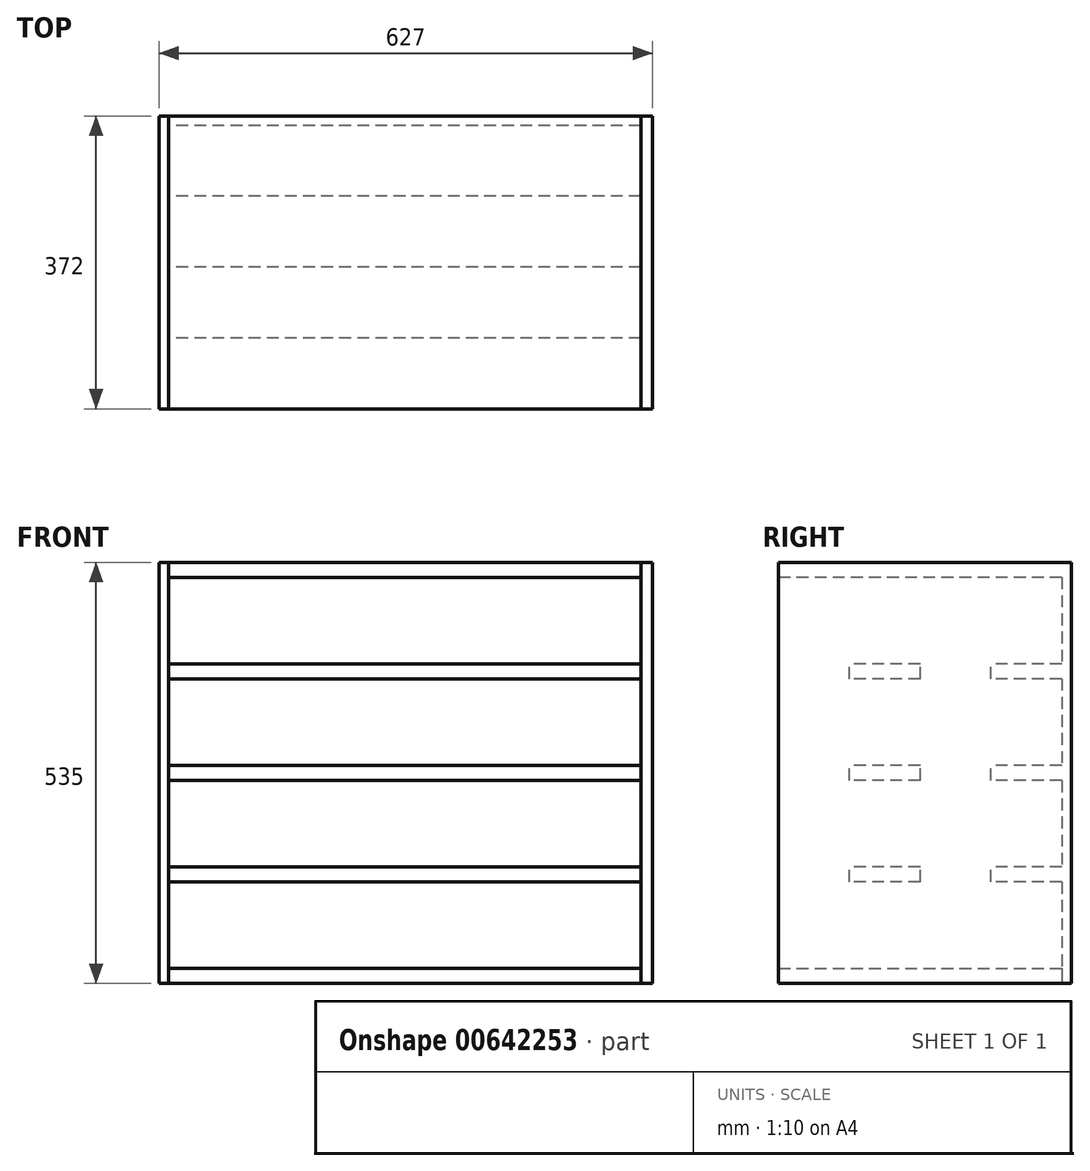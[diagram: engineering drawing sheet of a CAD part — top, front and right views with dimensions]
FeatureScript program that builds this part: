
annotation { "Feature Type Name" : "Feature", "Feature Type Description" : "" }
export const myFeature = defineFeature(function(context is Context, id is Id, definition is map)
    precondition{}
    {
        {
            var Q0;
            Q0=qCreatedBy(makeId("Right.planeOp"),FACE);
            var sketch = newSketch(context, id + "F0", { "sketchPlane" : qUnion([Q0])});
            skLineSegment(sketch, "E0.bottom", {"start": v(-360, 19) * mm, "end": v(0, 19) * mm});
            skLineSegment(sketch, "E0.top", {"start": v(-360, 0) * mm, "end": v(0, 0) * mm});
            skLineSegment(sketch, "E0.left", {"start": v(-360, 19) * mm, "end": v(-360, 0) * mm});
            skLineSegment(sketch, "E0.right", {"start": v(0, 19) * mm, "end": v(0, 0) * mm});
            skSolve(sketch);
        }
        {
            var Q0;
            Q0 = qSketchRegion(id + "F0", true);
            extrude(context, id + "F1", {"entities" : qUnion([Q0]), "depth" : 600 * mm, "offsetDistance" : 25.4 * mm});
        }
        {
            var Q0;
            Q0=qCreatedBy(makeId("Right.planeOp"),FACE);
            var sketch = newSketch(context, id + "F2", { "sketchPlane" : qUnion([Q0])});
            skLineSegment(sketch, "E1.bottom", {"start": v(0, 129) * mm, "end": v(-90, 129) * mm});
            skLineSegment(sketch, "E1.top", {"start": v(0, 148) * mm, "end": v(-90, 148) * mm});
            skLineSegment(sketch, "E1.right", {"start": v(-90, 129) * mm, "end": v(-90, 148) * mm});
            skLineSegment(sketch, "E2.0.1.0", {"start": v(-90, 258) * mm, "end": v(-90, 277) * mm});
            skLineSegment(sketch, "E2.0.1.1", {"start": v(0, 277) * mm, "end": v(-90, 277) * mm});
            skLineSegment(sketch, "E2.0.1.2", {"start": v(0, 258) * mm, "end": v(-90, 258) * mm});
            skLineSegment(sketch, "E2.0.2.0", {"start": v(-90, 387) * mm, "end": v(-90, 406) * mm});
            skLineSegment(sketch, "E2.0.2.1", {"start": v(0, 406) * mm, "end": v(-90, 406) * mm});
            skLineSegment(sketch, "E2.0.2.2", {"start": v(0, 387) * mm, "end": v(-90, 387) * mm});
            skLineSegment(sketch, "E2.1.0.0", {"start": v(-270, 129) * mm, "end": v(-270, 148) * mm});
            skLineSegment(sketch, "E2.1.0.1", {"start": v(-180, 148) * mm, "end": v(-270, 148) * mm});
            skLineSegment(sketch, "E2.1.0.2", {"start": v(-180, 129) * mm, "end": v(-270, 129) * mm});
            skLineSegment(sketch, "E2.1.0.3", {"start": v(-180, 129) * mm, "end": v(-180, 148) * mm});
            skLineSegment(sketch, "E2.1.1.0", {"start": v(-270, 258) * mm, "end": v(-270, 277) * mm});
            skLineSegment(sketch, "E2.1.1.1", {"start": v(-180, 277) * mm, "end": v(-270, 277) * mm});
            skLineSegment(sketch, "E2.1.1.2", {"start": v(-180, 258) * mm, "end": v(-270, 258) * mm});
            skLineSegment(sketch, "E2.1.1.3", {"start": v(-180, 258) * mm, "end": v(-180, 277) * mm});
            skLineSegment(sketch, "E2.1.2.0", {"start": v(-270, 387) * mm, "end": v(-270, 406) * mm});
            skLineSegment(sketch, "E2.1.2.1", {"start": v(-180, 406) * mm, "end": v(-270, 406) * mm});
            skLineSegment(sketch, "E2.1.2.2", {"start": v(-180, 387) * mm, "end": v(-270, 387) * mm});
            skLineSegment(sketch, "E2.1.2.3", {"start": v(-180, 387) * mm, "end": v(-180, 406) * mm});
            skLineSegment(sketch, "E2.direction1", {"start": v(-90, 129) * mm, "end": v(-270, 129) * mm, "construction": true});
            skLineSegment(sketch, "E2.direction2", {"start": v(-90, 129) * mm, "end": v(-90, 258) * mm, "construction": true});
            skLineSegment(sketch, "E3.bottom", {"start": v(0, 516) * mm, "end": v(-360, 516) * mm});
            skLineSegment(sketch, "E3.top", {"start": v(0, 535) * mm, "end": v(-360, 535) * mm});
            skLineSegment(sketch, "E3.right", {"start": v(-360, 516) * mm, "end": v(-360, 535) * mm});
            skLineSegment(sketch, "E4", {"start": v(0, 406) * mm, "end": v(0, 516) * mm, "construction": true});
            skLineSegment(sketch, "E5.bottom", {"start": v(0, 535) * mm, "end": v(12, 535) * mm});
            skLineSegment(sketch, "E5.top", {"start": v(0, 0) * mm, "end": v(12, 0) * mm});
            skLineSegment(sketch, "E5.left", {"start": v(0, 516) * mm, "end": v(0, 406) * mm});
            skLineSegment(sketch, "E5.right", {"start": v(12, 535) * mm, "end": v(12, 0) * mm});
            skLineSegment(sketch, "E6.trimOffspring", {"start": v(0, 387) * mm, "end": v(0, 277) * mm});
            skLineSegment(sketch, "E7.trimOffspring", {"start": v(0, 258) * mm, "end": v(0, 148) * mm});
            skLineSegment(sketch, "E8.trimOffspring", {"start": v(0, 129) * mm, "end": v(0, 0) * mm});
            skSolve(sketch);
        }
        {
            var Q0;
            Q0 = qSketchRegion(id + "F2", true);
            extrude(context, id + "F3", {"entities" : qUnion([Q0]), "depth" : 600 * mm, "offsetDistance" : 25 * mm});
        }
        {
            var Q0;
            Q0=qCreatedBy(makeId("Right.planeOp"),FACE);
            var sketch = newSketch(context, id + "F4", { "sketchPlane" : qUnion([Q0])});
            skLineSegment(sketch, "E9.bottom", {"start": v(-360, 535) * mm, "end": v(12, 535) * mm});
            skLineSegment(sketch, "E9.top", {"start": v(-360, 0) * mm, "end": v(12, 0) * mm});
            skLineSegment(sketch, "E9.left", {"start": v(-360, 535) * mm, "end": v(-360, 0) * mm});
            skLineSegment(sketch, "E9.right", {"start": v(12, 535) * mm, "end": v(12, 0) * mm});
            skSolve(sketch);
        }
        {
            var Q0;
            Q0 = qSketchRegion(id + "F4", true);
            extrude(context, id + "F5", {"entities" : qUnion([Q0]), "oppositeDirection" : true, "depth" : 12 * mm, "offsetDistance" : 25 * mm});
        }
        {
            var Q0;
            Q0=makeQuery(id+"F3.opExtrude","CAP_FACE",FACE,{"disambiguationData":[OSD([sQuery(id+"F2.wireOp",EDGE,"E1.bottom"),sQuery(id+"F2.wireOp",EDGE,"E1.top"),sQuery(id+"F2.wireOp",EDGE,"E1.right"),sQuery(id+"F2.wireOp",EDGE,"E2.0.1.0"),sQuery(id+"F2.wireOp",EDGE,"E2.0.1.1"),sQuery(id+"F2.wireOp",EDGE,"E2.0.1.2"),sQuery(id+"F2.wireOp",EDGE,"E2.0.2.0"),sQuery(id+"F2.wireOp",EDGE,"E2.0.2.1"),sQuery(id+"F2.wireOp",EDGE,"E2.0.2.2"),sQuery(id+"F2.wireOp",EDGE,"E3.bottom"),sQuery(id+"F2.wireOp",EDGE,"E3.top"),sQuery(id+"F2.wireOp",EDGE,"E3.right"),sQuery(id+"F2.wireOp",EDGE,"E5.bottom"),sQuery(id+"F2.wireOp",EDGE,"E5.top"),sQuery(id+"F2.wireOp",EDGE,"E5.left"),sQuery(id+"F2.wireOp",EDGE,"E5.right"),sQuery(id+"F2.wireOp",EDGE,"E6.trimOffspring"),sQuery(id+"F2.wireOp",EDGE,"E7.trimOffspring"),sQuery(id+"F2.wireOp",EDGE,"E8.trimOffspring")])],"isStart":false});
            var sketch = newSketch(context, id + "F6", { "sketchPlane" : qUnion([Q0])});
            skLineSegment(sketch, "E10.bottom", {"start": v(-360, 535) * mm, "end": v(12, 535) * mm});
            skLineSegment(sketch, "E10.top", {"start": v(-360, 0) * mm, "end": v(12, 0) * mm});
            skLineSegment(sketch, "E10.left", {"start": v(-360, 535) * mm, "end": v(-360, 0) * mm});
            skLineSegment(sketch, "E10.right", {"start": v(12, 535) * mm, "end": v(12, 0) * mm});
            skSolve(sketch);
        }
        {
            var Q0;
            Q0 = qSketchRegion(id + "F6", true);
            extrude(context, id + "F7", {"entities" : qUnion([Q0]), "depth" : 15 * mm, "offsetDistance" : 25 * mm});
        }
    });
